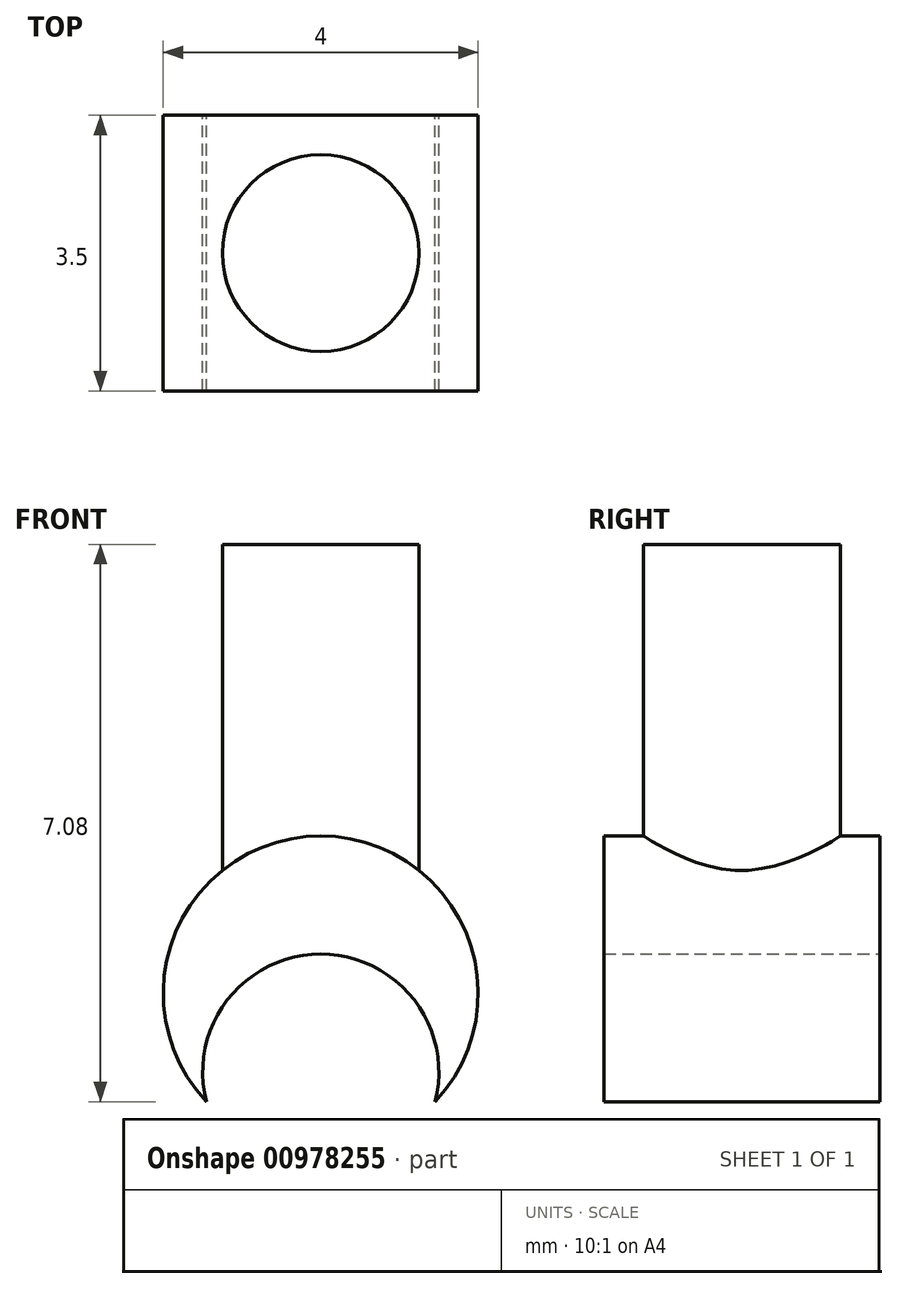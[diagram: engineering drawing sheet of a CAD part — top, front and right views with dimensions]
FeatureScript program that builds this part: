
annotation { "Feature Type Name" : "Feature", "Feature Type Description" : "" }
export const myFeature = defineFeature(function(context is Context, id is Id, definition is map)
    precondition{}
    {
        {
            var Q0;
            Q0=qCreatedBy(makeId("Front.planeOp"),FACE);
            var sketch = newSketch(context, id + "F0", { "sketchPlane" : qUnion([Q0])});
            skArc(sketch, "E0", {"start": v(1.45, -2.08) * mm, "mid": v(0, 1.3) * mm, "end": v(-1.45, -2.08) * mm});
            skArc(sketch, "E1", {"start": v(1.45, -2.08) * mm, "mid": v(0, -0.2) * mm, "end": v(-1.45, -2.08) * mm});
            skSolve(sketch);
        }
        {
            var Q0;
            Q0=makeQuery(id+"F0.imprint","IMPRINT",FACE,{"disambiguationData":[TD([[makeQuery(id+"F0.imprint","IMPRINT",EDGE,{"derivedFrom":sQuery(id+"F0.wireOp",EDGE,"E0")}),1.0]])]});
            extrude(context, id + "F1", {"entities" : qUnion([Q0]), "endBound" : BoundingType.SYMMETRIC, "depth" : 3.5 * mm, "offsetDistance" : 25.4 * mm});
        }
        {
            var Q0;
            Q0=qCreatedBy(makeId("Top.planeOp"),FACE);
            var sketch = newSketch(context, id + "F2", { "sketchPlane" : qUnion([Q0])});
            skCircle(sketch, "E2", {"center": v(0, 0) * mm, "radius": 1.25 * mm});
            skSolve(sketch);
        }
        {
            var Q0;
            Q0=qSketchRegion(id+"F2",true);
            extrude(context, id + "F3", {"entities" : qUnion([Q0]), "operationType" : NewBodyOperationType.ADD, "depth" : 5 * mm, "offsetDistance" : 25.4 * mm});
        }
    });
